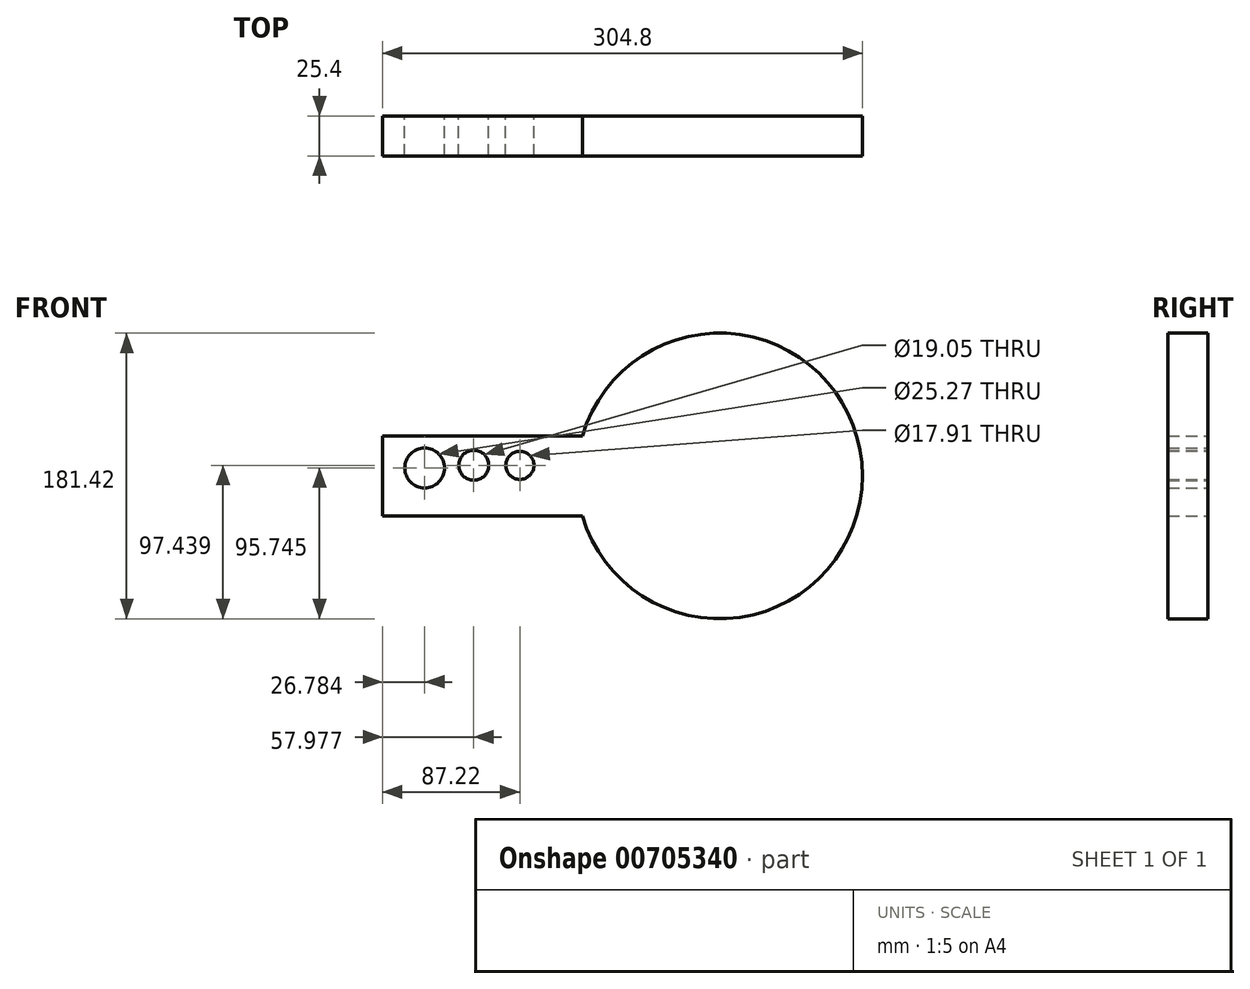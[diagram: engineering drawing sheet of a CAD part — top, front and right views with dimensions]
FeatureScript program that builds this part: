
annotation { "Feature Type Name" : "Feature", "Feature Type Description" : "" }
export const myFeature = defineFeature(function(context is Context, id is Id, definition is map)
    precondition{}
    {
        {
            var Q0;
            Q0=qCreatedBy(makeId("Front.planeOp"),FACE);
            var sketch = newSketch(context, id + "F0", { "sketchPlane" : qUnion([Q0])});
            skLineSegment(sketch, "E0", {"start": v(-122.4, 50.8) * mm, "end": v(4.6, 50.8) * mm});
            skLineSegment(sketch, "E1", {"start": v(4.6, 50.8) * mm, "end": v(4.6, 0) * mm});
            skLineSegment(sketch, "E2", {"start": v(4.6, 0) * mm, "end": v(-122.4, 0) * mm});
            skLineSegment(sketch, "E3", {"start": v(-122.4, 0) * mm, "end": v(-122.4, 50.8) * mm});
            skCircle(sketch, "E4", {"center": v(-95.63, 30.43) * mm, "radius": 12.64 * mm});
            skCircle(sketch, "E5", {"center": v(-64.43, 32.13) * mm, "radius": 9.53 * mm});
            skCircle(sketch, "E6", {"center": v(-35.19, 32.13) * mm, "radius": 8.95 * mm});
            skArc(sketch, "E7", {"start": v(4.6, 0) * mm, "mid": v(182.4, 25.4) * mm, "end": v(4.6, 50.8) * mm});
            skSolve(sketch);
        }
        {
            var Q0;
            Q0 = qSketchRegion(id + "F0", true);
            extrude(context, id + "F1", {"entities" : qUnion([Q0]), "depth" : 25.4 * mm, "offsetDistance" : 25.4 * mm});
        }
    });
